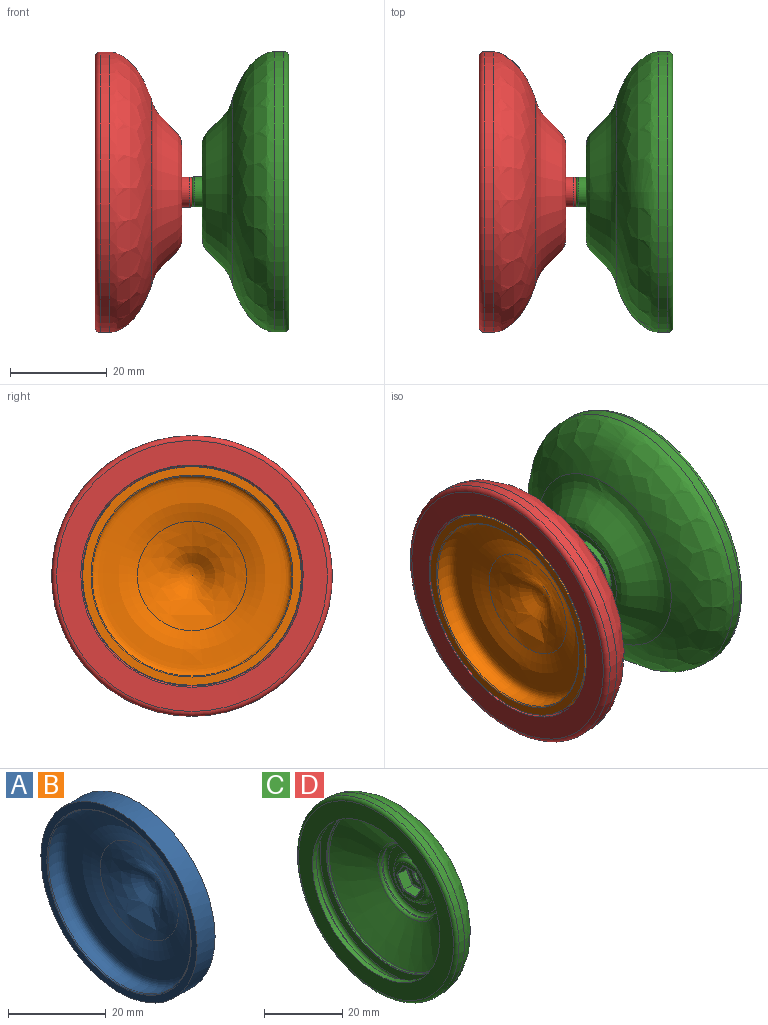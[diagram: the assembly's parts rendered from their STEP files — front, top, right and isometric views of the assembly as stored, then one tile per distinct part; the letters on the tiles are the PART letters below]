
ASSEMBLY  parts=4 mates=2
PART A: 6 faces, bbox 11.7x45.5x45.5 mm
  f0: revolved ~45.2x45.2mm, area 1663.3mm2, adj f1
  f1: cylinder r=22.6mm len=45.2mm, axis (1,0,0), area 738.4mm2, adj f0,f2
  f2: plane 45.2x45.2mm, normal (-1,0,0), area 234.5mm2, adj f1,f3
  f3: torus R=20.88mm, axis (1,0,0), area 49.3mm2, adj f2
  f4: revolved ~42.04x42.04mm, area 2880.9mm2, adj f5
  f5: revolved ~22.6x22.6mm, area 0mm2, adj f4
PART B: same geometry as A
PART C: 55 faces, bbox 20x62.8x62.8 mm
  f0: plane 10.64x10.64mm, normal (-1,0,0), area 33.4mm2, adj f3,f49,f50,f51,f52,f53,f54
  f1: cylinder r=2.1mm len=4.3mm, axis (1,0,0), area 56.7mm2, adj f4,f48
  f2: torus R=7.32mm, axis (1,0,0), area 65.9mm2, adj f3,f34
  f3: torus R=5.32mm, axis (1,0,0), area 58.8mm2, adj f0,f2
  f4: plane 5.2x5.2mm, normal (1,0,0), area 7.4mm2, adj f1,f5
  f5: torus R=2.6mm, axis (1,0,0), area 14.4mm2, adj f4,f6
  f6: cylinder r=3.1mm len=6.2mm, axis (1,0,0), area 34.1mm2, adj f5,f7
  f7: plane 8.2x8.2mm, normal (1,0,0), area 22.6mm2, adj f6,f8
  f8: cylinder r=4.1mm len=8.2mm, axis (1,0,0), area 11.6mm2, adj f7,f9
  f9: torus R=4.6mm, axis (1,0,0), area 21.1mm2, adj f8,f10
  f10: plane 12.39x12.39mm, normal (1,0,0), area 54.1mm2, adj f9,f11
  f11: torus R=6.2mm, axis (1,0,0), area 31.9mm2, adj f10,f12
  f12: cone r=6.69mm half-angle=0.5deg, axis (1,0,0), area 26.8mm2, adj f11,f13
  f13: plane 14x14mm, normal (1,0,0), area 12.9mm2, adj f12,f14
  f14: cone r=7mm half-angle=0.1deg, axis (-1,0,0), area 52.8mm2, adj f13,f15
  f15: plane 19.51x19.51mm, normal (1,0,0), area 144.8mm2, adj f14,f16
  f16: cone r=9.75mm half-angle=0.1deg, axis (-1,0,0), area 73.5mm2, adj f15,f17
  f17: revolved ~38.87x38.87mm, area 1087.2mm2, adj f16,f18
  f18: revolved ~58x58mm, area 2137mm2, adj f17,f19
  f19: cylinder r=29mm len=58mm, axis (1,0,0), area 361.9mm2, adj f18,f20
  f20: torus R=28mm, axis (1,0,0), area 282.6mm2, adj f19,f21
  f21: cone r=28mm half-angle=89.8deg, axis (-1,0,0), area 800.9mm2, adj f20,f22
  f22: cone r=23mm half-angle=0.2deg, axis (1,0,0), area 216.8mm2, adj f21,f23
  f23: plane 50.81x50.81mm, normal (1,0,0), area 365mm2, adj f22,f24
  f24: torus R=25.4mm, axis (1,0,0), area 257mm2, adj f23,f25
  f25: cylinder r=26.4mm len=52.81mm, axis (1,0,0), area 265.4mm2, adj f24,f26
  f26: torus R=25.4mm, axis (1,0,0), area 257mm2, adj f25,f27
  f27: plane 50.81x50.81mm, normal (-1,0,0), area 365.7mm2, adj f26,f28
  f28: cylinder r=23mm len=46mm, axis (1,0,0), area 42.5mm2, adj f27,f29
  f29: torus R=22.5mm, axis (1,0,0), area 79mm2, adj f28,f30
  f30: cone r=22.73mm half-angle=63.3deg, axis (-1,0,0), area 1385.6mm2, adj f29,f31
  f31: torus R=11.52mm, axis (1,0,0), area 74.3mm2, adj f30,f32
  f32: cylinder r=10.52mm len=21.05mm, axis (1,0,0), area 25.3mm2, adj f31,f33
  f33: torus R=9.52mm, axis (1,0,0), area 100.3mm2, adj f32,f34
  f34: plane 19.05x19.05mm, normal (-1,0,0), area 116.7mm2, adj f2,f33
  f35: plane 3.8x3.1mm, normal (0,0.87,0.5), area 13.6mm2, adj f36,f40,f45,f52
  f36: plane 3.8x3.1mm, normal (0,0.87,-0.5), area 13.6mm2, adj f35,f37,f43,f50
  f37: plane 4.39x3.1mm, normal (0,0,-1), area 13.6mm2, adj f36,f38,f42,f49
  f38: plane 3.8x3.1mm, normal (0,-0.87,-0.5), area 13.6mm2, adj f37,f39,f44,f51
  f39: plane 3.8x3.1mm, normal (0,-0.87,0.5), area 13.6mm2, adj f38,f40,f46,f53
  f40: plane 4.39x3.1mm, normal (0,0,1), area 13.6mm2, adj f35,f39,f47,f54
  f41: plane 8.31x7.2mm, normal (-1,0,0), area 28.3mm2, adj f42,f43,f44,f45,f46,f47,f48
  f42: cylinder r=0.2mm len=4.39mm, axis (0,1,0), area 1.4mm2, adj f37,f41,f43,f44
  f43: cylinder r=0.2mm len=3.9mm, axis (0,0.5,0.87), area 1.4mm2, adj f36,f41,f42,f45
  f44: cylinder r=0.2mm len=3.9mm, axis (0,0.5,-0.87), area 1.4mm2, adj f38,f41,f42,f46
  f45: cylinder r=0.2mm len=3.9mm, axis (0,-0.5,0.87), area 1.4mm2, adj f35,f41,f43,f47
  f46: cylinder r=0.2mm len=3.9mm, axis (0,-0.5,-0.87), area 1.4mm2, adj f39,f41,f44,f47
  f47: cylinder r=0.2mm len=4.39mm, axis (0,-1,0), area 1.4mm2, adj f40,f41,f45,f46
  f48: torus R=2.3mm, axis (-1,0,0), area 4.3mm2, adj f1,f41
  f49: cylinder r=0.2mm len=4.62mm, axis (0,-1,0), area 1.4mm2, adj f0,f37,f50,f51
  f50: cylinder r=0.2mm len=4.1mm, axis (0,-0.5,-0.87), area 1.4mm2, adj f0,f36,f49,f52
  f51: cylinder r=0.2mm len=4.1mm, axis (0,-0.5,0.87), area 1.4mm2, adj f0,f38,f49,f53
  f52: cylinder r=0.2mm len=4.1mm, axis (0,0.5,-0.87), area 1.4mm2, adj f0,f35,f50,f54
  f53: cylinder r=0.2mm len=4.1mm, axis (0,0.5,0.87), area 1.4mm2, adj f0,f39,f51,f54
  f54: cylinder r=0.2mm len=4.62mm, axis (0,1,0), area 1.4mm2, adj f0,f40,f52,f53
PART D: same geometry as C
PLACE A rot(axis=(0,1,0),180deg) t=(88.76,-0.13,-14.1)mm
PLACE B t=(-42.28,-0.13,-2.03)mm
PLACE C rot(axis=(0,1,0),180deg) t=(63.76,-0.13,-13.48)mm
PLACE D t=(-17.3,-0.13,-2.65)mm
MATE planar A.f1 <-> C.f1  axis (-1,0,0) through (43.24,-0.13,-8.07)mm
MATE planar C.f1 <-> D.f1  axis (-1,0,0) through (23.23,-0.13,-8.05)mm
